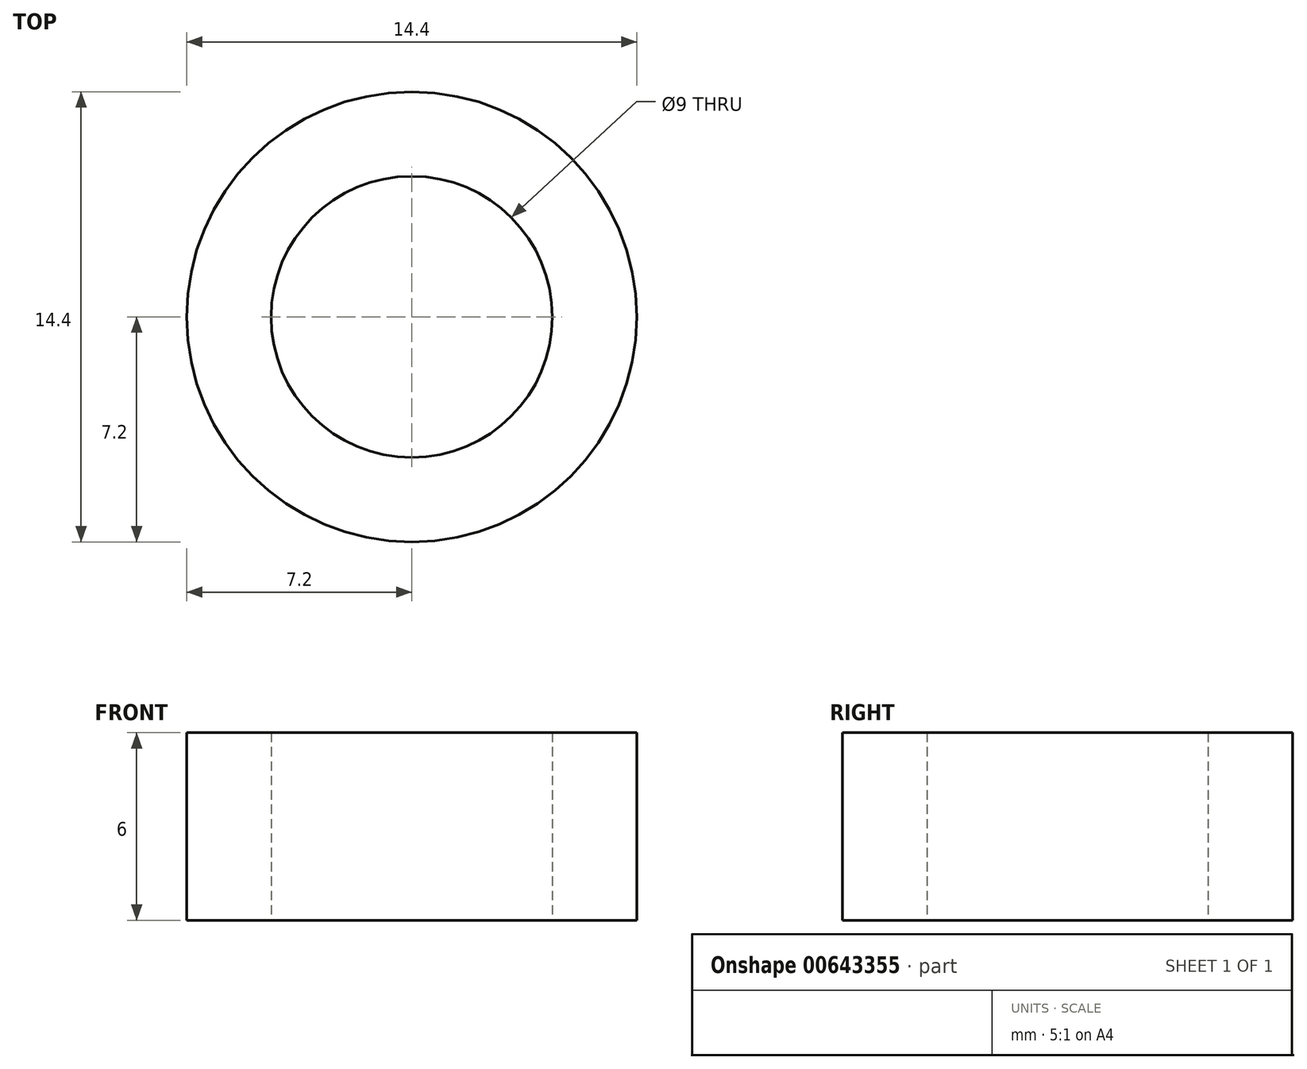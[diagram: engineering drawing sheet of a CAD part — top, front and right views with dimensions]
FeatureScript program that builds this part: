
annotation { "Feature Type Name" : "Feature", "Feature Type Description" : "" }
export const myFeature = defineFeature(function(context is Context, id is Id, definition is map)
    precondition{}
    {
        {
            var Q0;
            Q0=qCreatedBy(makeId("Top.planeOp"),FACE);
            var sketch = newSketch(context, id + "F0", { "sketchPlane" : qUnion([Q0])});
            skCircle(sketch, "E0", {"center": v(0, 0) * mm, "radius": 7.2 * mm});
            skCircle(sketch, "E1", {"center": v(0, 0) * mm, "radius": 4.5 * mm});
            skSolve(sketch);
        }
        {
            var Q0;
            Q0 = qSketchRegion(id + "F0", true);
            extrude(context, id + "F1", {"entities" : qUnion([Q0]), "depth" : 6 * mm, "offsetDistance" : 25 * mm});
        }
    });
